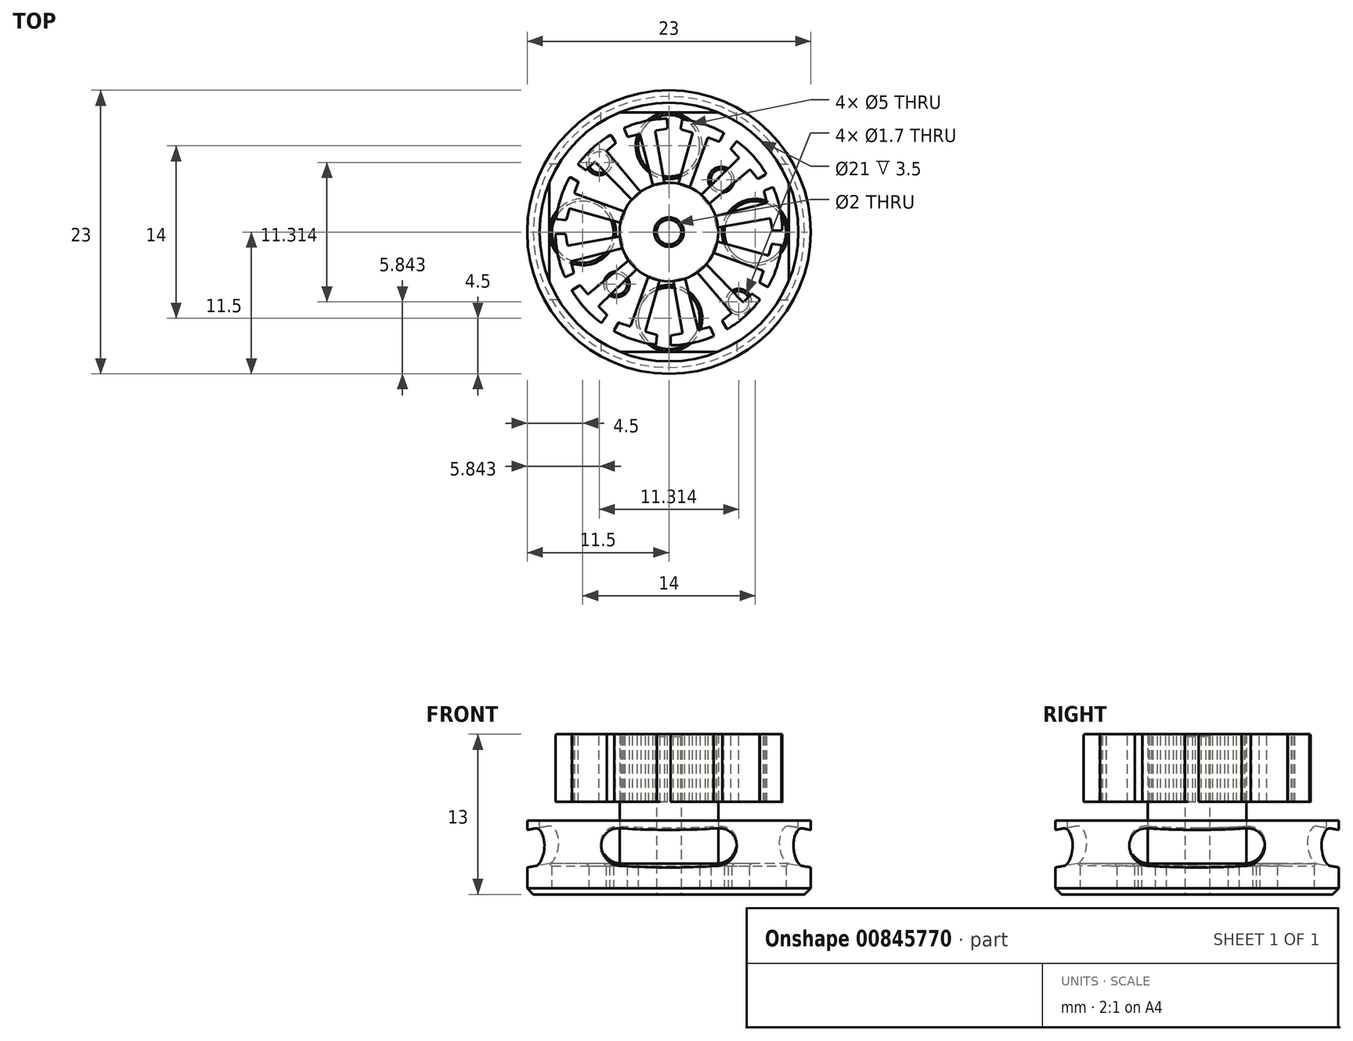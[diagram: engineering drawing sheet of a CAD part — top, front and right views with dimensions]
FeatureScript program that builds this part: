
annotation { "Feature Type Name" : "Feature", "Feature Type Description" : "" }
export const myFeature = defineFeature(function(context is Context, id is Id, definition is map)
    precondition{}
    {
        {
            var Q0;
            Q0=qCreatedBy(makeId("Top.planeOp"),FACE);
            var sketch = newSketch(context, id + "F0", { "sketchPlane" : qUnion([Q0])});
            skCircle(sketch, "E0", {"center": v(0, 0) * mm, "radius": 11.5 * mm});
            skSolve(sketch);
        }
        {
            var Q0;
            Q0 = qSketchRegion(id + "F0", true);
            extrude(context, id + "F1", {"entities" : qUnion([Q0]), "depth" : 6 * mm, "offsetDistance" : 25 * mm});
        }
        {
            var Q0;
            Q0=makeQuery(id+"F1.opExtrude","CAP_FACE",FACE,{"disambiguationData":[OSD([sQuery(id+"F0.wireOp",EDGE,"E0")])],"isStart":true});
            var sketch = newSketch(context, id + "F2", { "sketchPlane" : qUnion([Q0])});
            skCircle(sketch, "E1", {"center": v(0, 0) * mm, "radius": 1 * mm});
            skSolve(sketch);
        }
        {
            var Q0;
            Q0=makeQuery(id+"F1.opExtrude","CAP_EDGE",EDGE,{"disambiguationData":[OSD([sQuery(id+"F0.wireOp",EDGE,"E0")])],"isStart":true});
            chamfer(context, id + "F3", {"entities" : qUnion([Q0]), "width" : .5 * mm, "tangentPropagation" : true});
        }
        {
            var Q0;
            Q0=makeQuery(id+"F1.opExtrude","CAP_FACE",FACE,{"disambiguationData":[OSD([sQuery(id+"F0.wireOp",EDGE,"E0")])],"isStart":false});
            var sketch = newSketch(context, id + "F4", { "sketchPlane" : qUnion([Q0])});
            skCircle(sketch, "E2", {"center": v(0, 0) * mm, "radius": 10.5 * mm});
            skSolve(sketch);
        }
        {
            var Q0;
            Q0 = qSketchRegion(id + "F4", true);
            extrude(context, id + "F5", {"entities" : qUnion([Q0]), "operationType" : NewBodyOperationType.REMOVE, "oppositeDirection" : true, "depth" : 3.5 * mm, "offsetDistance" : 25 * mm});
        }
        {
            var Q0;
            Q0 = qSketchRegion(id + "F2", true);
            extrude(context, id + "F6", {"entities" : qUnion([Q0]), "operationType" : NewBodyOperationType.REMOVE, "endBound" : BoundingType.THROUGH_ALL, "oppositeDirection" : true, "depth" : 25 * mm, "offsetDistance" : 25 * mm});
        }
        {
            var Q0;
            Q0=makeQuery(id+"F1.opExtrude","CAP_FACE",FACE,{"disambiguationData":[OSD([sQuery(id+"F0.wireOp",EDGE,"E0")])],"isStart":true});
            var sketch = newSketch(context, id + "F7", { "sketchPlane" : qUnion([Q0])});
            skCircle(sketch, "E3", {"center": v(0, 7) * mm, "radius": 2.5 * mm});
            skCircle(sketch, "E4.1.0", {"center": v(-7, 0) * mm, "radius": 2.5 * mm});
            skCircle(sketch, "E4.2.0", {"center": v(0, -7) * mm, "radius": 2.5 * mm});
            skPoint(sketch, "E4.center", {"position": v(0, 0) * mm});
            skCircle(sketch, "E5.1.3.0", {"center": v(7, 0) * mm, "radius": 2.5 * mm});
            skSolve(sketch);
        }
        {
            var Q0;
            Q0 = qSketchRegion(id + "F7", true);
            extrude(context, id + "F8", {"entities" : qUnion([Q0]), "operationType" : NewBodyOperationType.REMOVE, "endBound" : BoundingType.THROUGH_ALL, "oppositeDirection" : true, "depth" : 25 * mm, "offsetDistance" : 25 * mm});
        }
        {
            var Q0;
            Q0=makeQuery(id+"F1.opExtrude","CAP_FACE",FACE,{"disambiguationData":[OSD([sQuery(id+"F0.wireOp",EDGE,"E0")])],"isStart":true});
            var sketch = newSketch(context, id + "F9", { "sketchPlane" : qUnion([Q0])});
            skCircle(sketch, "E6", {"center": v(4.24, -4.24) * mm, "radius": 0.85 * mm});
            skLineSegment(sketch, "E7", {"start": v(0, 0) * mm, "end": v(4.24, -4.24) * mm});
            skCircle(sketch, "E8.1.0", {"center": v(-4.24, 4.24) * mm, "radius": 0.85 * mm});
            skPoint(sketch, "E8.center", {"position": v(0, 0) * mm});
            skCircle(sketch, "E9", {"center": v(5.66, 5.66) * mm, "radius": 0.85 * mm});
            skLineSegment(sketch, "E10", {"start": v(0, 0) * mm, "end": v(5.66, 5.66) * mm});
            skCircle(sketch, "E11.1.0", {"center": v(-5.66, -5.66) * mm, "radius": 0.85 * mm});
            skSolve(sketch);
        }
        {
            var Q0;
            Q0=makeQuery(id+"F9.imprint","IMPRINT",FACE,{"disambiguationData":[TD([[makeQuery(id+"F9.imprint","IMPRINT",EDGE,{"derivedFrom":sQuery(id+"F9.wireOp",EDGE,"E8.1.0")}),1.0]])]});
            var Q1;
            Q1=makeQuery(id+"F9.imprint","IMPRINT",FACE,{"disambiguationData":[TD([[makeQuery(id+"F9.imprint","IMPRINT",EDGE,{"derivedFrom":sQuery(id+"F9.wireOp",EDGE,"E9")}),1.0]])]});
            var Q2;
            Q2=makeQuery(id+"F9.imprint","IMPRINT",FACE,{"disambiguationData":[TD([[makeQuery(id+"F9.imprint","IMPRINT",EDGE,{"derivedFrom":sQuery(id+"F9.wireOp",EDGE,"E6")}),1.0]])]});
            var Q3;
            Q3=makeQuery(id+"F9.imprint","IMPRINT",FACE,{"disambiguationData":[TD([[makeQuery(id+"F9.imprint","IMPRINT",EDGE,{"derivedFrom":sQuery(id+"F9.wireOp",EDGE,"E11.1.0")}),1.0]])]});
            var Q4;
            Q4=sQuery(id+"F9.wireOp",EDGE,"E6");
            extrude(context, id + "F10", {"entities" : qUnion([Q0, Q1, Q2, Q3]), "operationType" : NewBodyOperationType.REMOVE, "surfaceEntities" : qUnion([Q4]), "endBound" : BoundingType.THROUGH_ALL, "oppositeDirection" : true, "depth" : 25 * mm, "offsetDistance" : 25 * mm});
        }
        {
            var Q0;
            Q0=makeQuery(id+"F6.boolean.opBoolean","COPY",EDGE,{"derivedFrom":makeQuery(id+"F6.opExtrude","CAP_EDGE",EDGE,{"disambiguationData":[OSD([sQuery(id+"F2.wireOp",EDGE,"E1")])],"isStart":true})});
            var Q1;
            Q1=makeQuery(id+"F10.boolean.opBoolean","COPY",EDGE,{"derivedFrom":makeQuery(id+"F10.opExtrude","CAP_EDGE",EDGE,{"disambiguationData":[OSD([sQuery(id+"F9.wireOp",EDGE,"E6")])],"isStart":true})});
            var Q2;
            Q2=makeQuery(id+"F8.boolean.opBoolean","COPY",EDGE,{"derivedFrom":makeQuery(id+"F8.opExtrude","CAP_EDGE",EDGE,{"disambiguationData":[OSD([sQuery(id+"F7.wireOp",EDGE,"E5.1.3.0")])],"isStart":true})});
            var Q3;
            Q3=makeQuery(id+"F8.boolean.opBoolean","COPY",EDGE,{"derivedFrom":makeQuery(id+"F8.opExtrude","CAP_EDGE",EDGE,{"disambiguationData":[OSD([sQuery(id+"F7.wireOp",EDGE,"E3")])],"isStart":true})});
            var Q4;
            Q4=makeQuery(id+"F10.boolean.opBoolean","COPY",EDGE,{"derivedFrom":makeQuery(id+"F10.opExtrude","CAP_EDGE",EDGE,{"disambiguationData":[OSD([sQuery(id+"F9.wireOp",EDGE,"E8.1.0")])],"isStart":true})});
            var Q5;
            Q5=makeQuery(id+"F8.boolean.opBoolean","COPY",EDGE,{"derivedFrom":makeQuery(id+"F8.opExtrude","CAP_EDGE",EDGE,{"disambiguationData":[OSD([sQuery(id+"F7.wireOp",EDGE,"E4.1.0")])],"isStart":true})});
            var Q6;
            Q6=makeQuery(id+"F8.boolean.opBoolean","COPY",EDGE,{"derivedFrom":makeQuery(id+"F8.opExtrude","CAP_EDGE",EDGE,{"disambiguationData":[OSD([sQuery(id+"F7.wireOp",EDGE,"E4.2.0")])],"isStart":true})});
            var Q7;
            Q7=makeQuery(id+"F8.boolean.opBoolean","INTERSECT",EDGE,{"derivedFrom":[makeQuery(id+"F5.boolean.opBoolean","COPY",FACE,{"derivedFrom":makeQuery(id+"F5.opExtrude","CAP_FACE",FACE,{"disambiguationData":[OSD([sQuery(id+"F4.wireOp",EDGE,"E2")])],"isStart":false})}),makeQuery(id+"F8.opExtrude","SWEPT_FACE",FACE,{"disambiguationData":[OSD([sQuery(id+"F7.wireOp",EDGE,"E4.1.0")])]})]});
            var Q8;
            Q8=makeQuery(id+"F10.boolean.opBoolean","INTERSECT",EDGE,{"derivedFrom":[makeQuery(id+"F5.boolean.opBoolean","COPY",FACE,{"derivedFrom":makeQuery(id+"F5.opExtrude","CAP_FACE",FACE,{"disambiguationData":[OSD([sQuery(id+"F4.wireOp",EDGE,"E2")])],"isStart":false})}),makeQuery(id+"F10.opExtrude","SWEPT_FACE",FACE,{"disambiguationData":[OSD([sQuery(id+"F9.wireOp",EDGE,"E8.1.0")])]})]});
            var Q9;
            Q9=makeQuery(id+"F8.boolean.opBoolean","INTERSECT",EDGE,{"derivedFrom":[makeQuery(id+"F5.boolean.opBoolean","COPY",FACE,{"derivedFrom":makeQuery(id+"F5.opExtrude","CAP_FACE",FACE,{"disambiguationData":[OSD([sQuery(id+"F4.wireOp",EDGE,"E2")])],"isStart":false})}),makeQuery(id+"F8.opExtrude","SWEPT_FACE",FACE,{"disambiguationData":[OSD([sQuery(id+"F7.wireOp",EDGE,"E4.2.0")])]})]});
            var Q10;
            Q10=makeQuery(id+"F10.boolean.opBoolean","INTERSECT",EDGE,{"derivedFrom":[makeQuery(id+"F5.boolean.opBoolean","COPY",FACE,{"derivedFrom":makeQuery(id+"F5.opExtrude","CAP_FACE",FACE,{"disambiguationData":[OSD([sQuery(id+"F4.wireOp",EDGE,"E2")])],"isStart":false})}),makeQuery(id+"F10.opExtrude","SWEPT_FACE",FACE,{"disambiguationData":[OSD([sQuery(id+"F9.wireOp",EDGE,"E6")])]})]});
            var Q11;
            Q11=makeQuery(id+"F8.boolean.opBoolean","INTERSECT",EDGE,{"derivedFrom":[makeQuery(id+"F5.boolean.opBoolean","COPY",FACE,{"derivedFrom":makeQuery(id+"F5.opExtrude","CAP_FACE",FACE,{"disambiguationData":[OSD([sQuery(id+"F4.wireOp",EDGE,"E2")])],"isStart":false})}),makeQuery(id+"F8.opExtrude","SWEPT_FACE",FACE,{"disambiguationData":[OSD([sQuery(id+"F7.wireOp",EDGE,"E5.1.3.0")])]})]});
            var Q12;
            Q12=makeQuery(id+"F8.boolean.opBoolean","INTERSECT",EDGE,{"derivedFrom":[makeQuery(id+"F5.boolean.opBoolean","COPY",FACE,{"derivedFrom":makeQuery(id+"F5.opExtrude","CAP_FACE",FACE,{"disambiguationData":[OSD([sQuery(id+"F4.wireOp",EDGE,"E2")])],"isStart":false})}),makeQuery(id+"F8.opExtrude","SWEPT_FACE",FACE,{"disambiguationData":[OSD([sQuery(id+"F7.wireOp",EDGE,"E3")])]})]});
            var Q13;
            Q13=makeQuery(id+"F10.boolean.opBoolean","COPY",EDGE,{"derivedFrom":makeQuery(id+"F10.opExtrude","CAP_EDGE",EDGE,{"disambiguationData":[OSD([sQuery(id+"F9.wireOp",EDGE,"E11.1.0")])],"isStart":true})});
            var Q14;
            Q14=makeQuery(id+"F10.boolean.opBoolean","COPY",EDGE,{"derivedFrom":makeQuery(id+"F10.opExtrude","CAP_EDGE",EDGE,{"disambiguationData":[OSD([sQuery(id+"F9.wireOp",EDGE,"E9")])],"isStart":true})});
            var Q15;
            Q15=makeQuery(id+"F10.boolean.opBoolean","INTERSECT",EDGE,{"derivedFrom":[makeQuery(id+"F5.boolean.opBoolean","COPY",FACE,{"derivedFrom":makeQuery(id+"F5.opExtrude","CAP_FACE",FACE,{"disambiguationData":[OSD([sQuery(id+"F4.wireOp",EDGE,"E2")])],"isStart":false})}),makeQuery(id+"F10.opExtrude","SWEPT_FACE",FACE,{"disambiguationData":[OSD([sQuery(id+"F9.wireOp",EDGE,"E9")])]})]});
            var Q16;
            Q16=makeQuery(id+"F10.boolean.opBoolean","INTERSECT",EDGE,{"derivedFrom":[makeQuery(id+"F5.boolean.opBoolean","COPY",FACE,{"derivedFrom":makeQuery(id+"F5.opExtrude","CAP_FACE",FACE,{"disambiguationData":[OSD([sQuery(id+"F4.wireOp",EDGE,"E2")])],"isStart":false})}),makeQuery(id+"F10.opExtrude","SWEPT_FACE",FACE,{"disambiguationData":[OSD([sQuery(id+"F9.wireOp",EDGE,"E11.1.0")])]})]});
            chamfer(context, id + "F11", {"entities" : qUnion([Q0, Q1, Q2, Q3, Q4, Q5, Q6, Q7, Q8, Q9, Q10, Q11, Q12, Q13, Q14, Q15, Q16]), "width" : .2 * mm, "tangentPropagation" : true});
        }
        {
            var Q0;
            Q0=makeQuery(id+"F1.opExtrude","CAP_FACE",FACE,{"disambiguationData":[OSD([sQuery(id+"F0.wireOp",EDGE,"E0")])],"isStart":true});
            var sketch = newSketch(context, id + "F12", { "sketchPlane" : qUnion([Q0])});
            skCircle(sketch, "E12", {"center": v(0, 0) * mm, "radius": 4 * mm});
            skSolve(sketch);
        }
        {
            var Q0;
            Q0 = qSketchRegion(id + "F12", true);
            extrude(context, id + "F13", {"entities" : qUnion([Q0]), "operationType" : NewBodyOperationType.ADD, "depth" : -13 * mm, "offsetDistance" : 25 * mm});
        }
        {
            var Q0;
            Q0 = qSketchRegion(id + "F2", true);
            extrude(context, id + "F14", {"entities" : qUnion([Q0]), "operationType" : NewBodyOperationType.REMOVE, "endBound" : BoundingType.THROUGH_ALL, "oppositeDirection" : true, "depth" : 25 * mm, "offsetDistance" : 25 * mm});
        }
        {
            var Q0;
            Q0=makeQuery(id+"F14.boolean.opBoolean","COPY",EDGE,{"derivedFrom":makeQuery(id+"F14.opExtrude","CAP_EDGE",EDGE,{"disambiguationData":[OSD([sQuery(id+"F2.wireOp",EDGE,"E1")])],"isStart":true})});
            var Q1;
            Q1=makeQuery(id+"F14.boolean.opBoolean","INTERSECT",EDGE,{"derivedFrom":[makeQuery(id+"F13.opExtrude","CAP_FACE",FACE,{"disambiguationData":[OSD([sQuery(id+"F12.wireOp",EDGE,"E12")])],"isStart":false}),makeQuery(id+"F14.opExtrude","SWEPT_FACE",FACE,{"disambiguationData":[OSD([sQuery(id+"F2.wireOp",EDGE,"E1")])]})]});
            chamfer(context, id + "F15", {"entities" : qUnion([Q0, Q1]), "width" : .2 * mm, "tangentPropagation" : true});
        }
        {
            var Q0;
            Q0=makeQuery(id+"F13.opExtrude","CAP_FACE",FACE,{"disambiguationData":[OSD([sQuery(id+"F12.wireOp",EDGE,"E12")])],"isStart":false});
            var sketch = newSketch(context, id + "F16", { "sketchPlane" : qUnion([Q0])});
            skLineSegment(sketch, "E13", {"start": v(-3.84, 0.73) * mm, "end": v(-7.98, 1.9) * mm});
            skLineSegment(sketch, "E14", {"start": v(-8.1, 1.83) * mm, "end": v(-8.32, 1.04) * mm});
            skLineSegment(sketch, "E15", {"start": v(-7.64, 3.25) * mm, "end": v(-7.37, 4.01) * mm});
            skArc(sketch, "E16", {"start": v(-8.08, 4.4) * mm, "mid": v(-8.76, 2.82) * mm, "end": v(-9.13, 1.15) * mm});
            skLineSegment(sketch, "E17", {"start": v(-8.43, 0.97) * mm, "end": v(-9.04, 1.04) * mm});
            skLineSegment(sketch, "E18", {"start": v(-7.41, 4.13) * mm, "end": v(-7.95, 4.43) * mm});
            skLineSegment(sketch, "E19", {"start": v(-3.54, 1.65) * mm, "end": v(-3.84, 0.73) * mm});
            skLineSegment(sketch, "E20", {"start": v(-7.58, 3.12) * mm, "end": v(-3.54, 1.65) * mm});
            skPoint(sketch, "E21.visualSharp", {"position": v(-9.14, 1.05) * mm});
            skArc(sketch, "E21.filletArc", {"start": v(-9.13, 1.15) * mm, "mid": v(-9.1, 1.08) * mm, "end": v(-9.04, 1.04) * mm});
            skPoint(sketch, "E22.visualSharp", {"position": v(-8.34, 0.96) * mm});
            skArc(sketch, "E22.filletArc", {"start": v(-8.43, 0.97) * mm, "mid": v(-8.36, 0.99) * mm, "end": v(-8.32, 1.04) * mm});
            skPoint(sketch, "E23.visualSharp", {"position": v(-8.07, 1.93) * mm});
            skArc(sketch, "E23.filletArc", {"start": v(-7.98, 1.9) * mm, "mid": v(-8.05, 1.89) * mm, "end": v(-8.1, 1.83) * mm});
            skPoint(sketch, "E24.visualSharp", {"position": v(-7.68, 3.15) * mm});
            skArc(sketch, "E24.filletArc", {"start": v(-7.64, 3.25) * mm, "mid": v(-7.64, 3.17) * mm, "end": v(-7.58, 3.12) * mm});
            skPoint(sketch, "E25.visualSharp", {"position": v(-7.34, 4.1) * mm});
            skArc(sketch, "E25.filletArc", {"start": v(-7.37, 4.01) * mm, "mid": v(-7.37, 4.08) * mm, "end": v(-7.41, 4.13) * mm});
            skPoint(sketch, "E26.visualSharp", {"position": v(-8.04, 4.48) * mm});
            skArc(sketch, "E26.filletArc", {"start": v(-7.95, 4.43) * mm, "mid": v(-8.02, 4.44) * mm, "end": v(-8.08, 4.4) * mm});
            skLineSegment(sketch, "E27.1.0", {"start": v(-8.13, -1.1) * mm, "end": v(-3.9, -0.35) * mm});
            skArc(sketch, "E27.1.1", {"start": v(-7.86, -2.35) * mm, "mid": v(-7.92, -2.4) * mm, "end": v(-7.93, -2.47) * mm});
            skLineSegment(sketch, "E27.1.2", {"start": v(-3.9, -0.35) * mm, "end": v(-3.7, -1.28) * mm});
            skLineSegment(sketch, "E27.1.3", {"start": v(-3.7, -1.28) * mm, "end": v(-7.86, -2.35) * mm});
            skLineSegment(sketch, "E27.1.4", {"start": v(-7.93, -2.47) * mm, "end": v(-7.73, -3.26) * mm});
            skPoint(sketch, "E27.1.5", {"position": v(-7.7, -3.34) * mm});
            skArc(sketch, "E27.1.6", {"start": v(-7.79, -3.37) * mm, "mid": v(-7.74, -3.33) * mm, "end": v(-7.73, -3.26) * mm});
            skLineSegment(sketch, "E27.1.7", {"start": v(-7.79, -3.37) * mm, "end": v(-8.35, -3.62) * mm});
            skArc(sketch, "E27.1.8", {"start": v(-8.48, -3.56) * mm, "mid": v(-8.43, -3.62) * mm, "end": v(-8.35, -3.62) * mm});
            skArc(sketch, "E27.1.9", {"start": v(-9.2, -0.24) * mm, "mid": v(-9, -1.93) * mm, "end": v(-8.48, -3.56) * mm});
            skArc(sketch, "E27.1.10", {"start": v(-9.1, -0.14) * mm, "mid": v(-9.17, -0.17) * mm, "end": v(-9.2, -0.24) * mm});
            skLineSegment(sketch, "E27.1.11", {"start": v(-8.48, -0.13) * mm, "end": v(-9.1, -0.14) * mm});
            skArc(sketch, "E27.1.12", {"start": v(-8.38, -0.2) * mm, "mid": v(-8.42, -0.15) * mm, "end": v(-8.48, -0.13) * mm});
            skLineSegment(sketch, "E27.1.13", {"start": v(-8.24, -1.01) * mm, "end": v(-8.38, -0.2) * mm});
            skArc(sketch, "E27.1.14", {"start": v(-8.24, -1.01) * mm, "mid": v(-8.2, -1.08) * mm, "end": v(-8.13, -1.1) * mm});
            skLineSegment(sketch, "E27.2.0", {"start": v(-6.5, -5) * mm, "end": v(-3.2, -2.25) * mm});
            skArc(sketch, "E27.2.1", {"start": v(-5.63, -5.96) * mm, "mid": v(-5.66, -6.03) * mm, "end": v(-5.63, -6.1) * mm});
            skLineSegment(sketch, "E27.2.2", {"start": v(-3.2, -2.25) * mm, "end": v(-2.55, -2.96) * mm});
            skLineSegment(sketch, "E27.2.3", {"start": v(-2.55, -2.96) * mm, "end": v(-5.63, -5.96) * mm});
            skLineSegment(sketch, "E27.2.4", {"start": v(-5.63, -6.1) * mm, "end": v(-5.07, -6.68) * mm});
            skPoint(sketch, "E27.2.5", {"position": v(-5, -6.75) * mm});
            skArc(sketch, "E27.2.6", {"start": v(-5.06, -6.81) * mm, "mid": v(-5.04, -6.75) * mm, "end": v(-5.07, -6.68) * mm});
            skLineSegment(sketch, "E27.2.7", {"start": v(-5.06, -6.81) * mm, "end": v(-5.42, -7.3) * mm});
            skArc(sketch, "E27.2.8", {"start": v(-5.56, -7.33) * mm, "mid": v(-5.49, -7.35) * mm, "end": v(-5.42, -7.3) * mm});
            skArc(sketch, "E27.2.9", {"start": v(-7.85, -4.8) * mm, "mid": v(-6.82, -6.17) * mm, "end": v(-5.56, -7.33) * mm});
            skArc(sketch, "E27.2.10", {"start": v(-7.81, -4.67) * mm, "mid": v(-7.86, -4.73) * mm, "end": v(-7.85, -4.8) * mm});
            skLineSegment(sketch, "E27.2.11", {"start": v(-7.28, -4.35) * mm, "end": v(-7.81, -4.67) * mm});
            skArc(sketch, "E27.2.12", {"start": v(-7.16, -4.37) * mm, "mid": v(-7.22, -4.34) * mm, "end": v(-7.28, -4.35) * mm});
            skLineSegment(sketch, "E27.2.13", {"start": v(-6.63, -5) * mm, "end": v(-7.16, -4.37) * mm});
            skArc(sketch, "E27.2.14", {"start": v(-6.63, -5) * mm, "mid": v(-6.56, -5.03) * mm, "end": v(-6.5, -5) * mm});
            skLineSegment(sketch, "E28.1.3.0", {"start": v(-3.12, -7.58) * mm, "end": v(-1.65, -3.54) * mm});
            skArc(sketch, "E28.3.3.0", {"start": v(-1.9, -7.98) * mm, "mid": v(-1.89, -8.05) * mm, "end": v(-1.83, -8.1) * mm});
            skLineSegment(sketch, "E28.7.3.0", {"start": v(-1.65, -3.54) * mm, "end": v(-0.73, -3.84) * mm});
            skLineSegment(sketch, "E28.10.3.0", {"start": v(-0.73, -3.84) * mm, "end": v(-1.9, -7.98) * mm});
            skLineSegment(sketch, "E28.13.3.0", {"start": v(-1.83, -8.1) * mm, "end": v(-1.04, -8.32) * mm});
            skPoint(sketch, "E28.16.3.0", {"position": v(-0.96, -8.34) * mm});
            skArc(sketch, "E28.17.3.0", {"start": v(-0.97, -8.43) * mm, "mid": v(-0.99, -8.36) * mm, "end": v(-1.04, -8.32) * mm});
            skLineSegment(sketch, "E28.21.3.0", {"start": v(-0.97, -8.43) * mm, "end": v(-1.04, -9.04) * mm});
            skArc(sketch, "E28.24.3.0", {"start": v(-1.15, -9.13) * mm, "mid": v(-1.08, -9.1) * mm, "end": v(-1.04, -9.04) * mm});
            skArc(sketch, "E28.28.3.0", {"start": v(-4.4, -8.08) * mm, "mid": v(-2.82, -8.76) * mm, "end": v(-1.15, -9.13) * mm});
            skArc(sketch, "E28.32.3.0", {"start": v(-4.43, -7.95) * mm, "mid": v(-4.44, -8.02) * mm, "end": v(-4.4, -8.08) * mm});
            skLineSegment(sketch, "E28.36.3.0", {"start": v(-4.13, -7.41) * mm, "end": v(-4.43, -7.95) * mm});
            skArc(sketch, "E28.39.3.0", {"start": v(-4.01, -7.37) * mm, "mid": v(-4.08, -7.37) * mm, "end": v(-4.13, -7.41) * mm});
            skLineSegment(sketch, "E28.43.3.0", {"start": v(-3.25, -7.64) * mm, "end": v(-4.01, -7.37) * mm});
            skArc(sketch, "E28.46.3.0", {"start": v(-3.25, -7.64) * mm, "mid": v(-3.17, -7.64) * mm, "end": v(-3.12, -7.58) * mm});
            skLineSegment(sketch, "E28.1.4.0", {"start": v(1.1, -8.13) * mm, "end": v(0.35, -3.9) * mm});
            skArc(sketch, "E28.3.4.0", {"start": v(2.35, -7.86) * mm, "mid": v(2.4, -7.92) * mm, "end": v(2.47, -7.93) * mm});
            skLineSegment(sketch, "E28.7.4.0", {"start": v(0.35, -3.9) * mm, "end": v(1.28, -3.7) * mm});
            skLineSegment(sketch, "E28.10.4.0", {"start": v(1.28, -3.7) * mm, "end": v(2.35, -7.86) * mm});
            skLineSegment(sketch, "E28.13.4.0", {"start": v(2.47, -7.93) * mm, "end": v(3.26, -7.73) * mm});
            skPoint(sketch, "E28.16.4.0", {"position": v(3.34, -7.7) * mm});
            skArc(sketch, "E28.17.4.0", {"start": v(3.37, -7.79) * mm, "mid": v(3.33, -7.74) * mm, "end": v(3.26, -7.73) * mm});
            skLineSegment(sketch, "E28.21.4.0", {"start": v(3.37, -7.79) * mm, "end": v(3.62, -8.35) * mm});
            skArc(sketch, "E28.24.4.0", {"start": v(3.56, -8.48) * mm, "mid": v(3.62, -8.43) * mm, "end": v(3.62, -8.35) * mm});
            skArc(sketch, "E28.28.4.0", {"start": v(0.24, -9.2) * mm, "mid": v(1.93, -9) * mm, "end": v(3.56, -8.48) * mm});
            skArc(sketch, "E28.32.4.0", {"start": v(0.14, -9.1) * mm, "mid": v(0.17, -9.17) * mm, "end": v(0.24, -9.2) * mm});
            skLineSegment(sketch, "E28.36.4.0", {"start": v(0.13, -8.48) * mm, "end": v(0.14, -9.1) * mm});
            skArc(sketch, "E28.39.4.0", {"start": v(0.2, -8.38) * mm, "mid": v(0.15, -8.42) * mm, "end": v(0.13, -8.48) * mm});
            skLineSegment(sketch, "E28.43.4.0", {"start": v(1.01, -8.24) * mm, "end": v(0.2, -8.38) * mm});
            skArc(sketch, "E28.46.4.0", {"start": v(1.01, -8.24) * mm, "mid": v(1.08, -8.2) * mm, "end": v(1.1, -8.13) * mm});
            skLineSegment(sketch, "E28.1.5.0", {"start": v(5, -6.5) * mm, "end": v(2.25, -3.2) * mm});
            skArc(sketch, "E28.3.5.0", {"start": v(5.96, -5.63) * mm, "mid": v(6.03, -5.66) * mm, "end": v(6.1, -5.63) * mm});
            skLineSegment(sketch, "E28.7.5.0", {"start": v(2.25, -3.2) * mm, "end": v(2.96, -2.55) * mm});
            skLineSegment(sketch, "E28.10.5.0", {"start": v(2.96, -2.55) * mm, "end": v(5.96, -5.63) * mm});
            skLineSegment(sketch, "E28.13.5.0", {"start": v(6.1, -5.63) * mm, "end": v(6.68, -5.07) * mm});
            skPoint(sketch, "E28.16.5.0", {"position": v(6.75, -5) * mm});
            skArc(sketch, "E28.17.5.0", {"start": v(6.81, -5.06) * mm, "mid": v(6.75, -5.04) * mm, "end": v(6.68, -5.07) * mm});
            skLineSegment(sketch, "E28.21.5.0", {"start": v(6.81, -5.06) * mm, "end": v(7.3, -5.42) * mm});
            skArc(sketch, "E28.24.5.0", {"start": v(7.33, -5.56) * mm, "mid": v(7.35, -5.49) * mm, "end": v(7.3, -5.42) * mm});
            skArc(sketch, "E28.28.5.0", {"start": v(4.8, -7.85) * mm, "mid": v(6.17, -6.82) * mm, "end": v(7.33, -5.56) * mm});
            skArc(sketch, "E28.32.5.0", {"start": v(4.67, -7.81) * mm, "mid": v(4.73, -7.86) * mm, "end": v(4.8, -7.85) * mm});
            skLineSegment(sketch, "E28.36.5.0", {"start": v(4.35, -7.28) * mm, "end": v(4.67, -7.81) * mm});
            skArc(sketch, "E28.39.5.0", {"start": v(4.37, -7.16) * mm, "mid": v(4.34, -7.22) * mm, "end": v(4.35, -7.28) * mm});
            skLineSegment(sketch, "E28.43.5.0", {"start": v(5, -6.63) * mm, "end": v(4.37, -7.16) * mm});
            skArc(sketch, "E28.46.5.0", {"start": v(5, -6.63) * mm, "mid": v(5.03, -6.56) * mm, "end": v(5, -6.5) * mm});
            skLineSegment(sketch, "E28.1.6.0", {"start": v(7.58, -3.12) * mm, "end": v(3.54, -1.65) * mm});
            skArc(sketch, "E28.3.6.0", {"start": v(7.98, -1.9) * mm, "mid": v(8.05, -1.89) * mm, "end": v(8.1, -1.83) * mm});
            skLineSegment(sketch, "E28.7.6.0", {"start": v(3.54, -1.65) * mm, "end": v(3.84, -0.73) * mm});
            skLineSegment(sketch, "E28.10.6.0", {"start": v(3.84, -0.73) * mm, "end": v(7.98, -1.9) * mm});
            skLineSegment(sketch, "E28.13.6.0", {"start": v(8.1, -1.83) * mm, "end": v(8.32, -1.04) * mm});
            skPoint(sketch, "E28.16.6.0", {"position": v(8.34, -0.96) * mm});
            skArc(sketch, "E28.17.6.0", {"start": v(8.43, -0.97) * mm, "mid": v(8.36, -0.99) * mm, "end": v(8.32, -1.04) * mm});
            skLineSegment(sketch, "E28.21.6.0", {"start": v(8.43, -0.97) * mm, "end": v(9.04, -1.04) * mm});
            skArc(sketch, "E28.24.6.0", {"start": v(9.13, -1.15) * mm, "mid": v(9.1, -1.08) * mm, "end": v(9.04, -1.04) * mm});
            skArc(sketch, "E28.28.6.0", {"start": v(8.08, -4.4) * mm, "mid": v(8.76, -2.82) * mm, "end": v(9.13, -1.15) * mm});
            skArc(sketch, "E28.32.6.0", {"start": v(7.95, -4.43) * mm, "mid": v(8.02, -4.44) * mm, "end": v(8.08, -4.4) * mm});
            skLineSegment(sketch, "E28.36.6.0", {"start": v(7.41, -4.13) * mm, "end": v(7.95, -4.43) * mm});
            skArc(sketch, "E28.39.6.0", {"start": v(7.37, -4.01) * mm, "mid": v(7.37, -4.08) * mm, "end": v(7.41, -4.13) * mm});
            skLineSegment(sketch, "E28.43.6.0", {"start": v(7.64, -3.25) * mm, "end": v(7.37, -4.01) * mm});
            skArc(sketch, "E28.46.6.0", {"start": v(7.64, -3.25) * mm, "mid": v(7.64, -3.17) * mm, "end": v(7.58, -3.12) * mm});
            skLineSegment(sketch, "E28.1.7.0", {"start": v(8.13, 1.1) * mm, "end": v(3.9, 0.35) * mm});
            skArc(sketch, "E28.3.7.0", {"start": v(7.86, 2.35) * mm, "mid": v(7.92, 2.4) * mm, "end": v(7.93, 2.47) * mm});
            skLineSegment(sketch, "E28.7.7.0", {"start": v(3.9, 0.35) * mm, "end": v(3.7, 1.28) * mm});
            skLineSegment(sketch, "E28.10.7.0", {"start": v(3.7, 1.28) * mm, "end": v(7.86, 2.35) * mm});
            skLineSegment(sketch, "E28.13.7.0", {"start": v(7.93, 2.47) * mm, "end": v(7.73, 3.26) * mm});
            skPoint(sketch, "E28.16.7.0", {"position": v(7.7, 3.34) * mm});
            skArc(sketch, "E28.17.7.0", {"start": v(7.79, 3.37) * mm, "mid": v(7.74, 3.33) * mm, "end": v(7.73, 3.26) * mm});
            skLineSegment(sketch, "E28.21.7.0", {"start": v(7.79, 3.37) * mm, "end": v(8.35, 3.62) * mm});
            skArc(sketch, "E28.24.7.0", {"start": v(8.48, 3.56) * mm, "mid": v(8.43, 3.62) * mm, "end": v(8.35, 3.62) * mm});
            skArc(sketch, "E28.28.7.0", {"start": v(9.2, 0.24) * mm, "mid": v(9, 1.93) * mm, "end": v(8.48, 3.56) * mm});
            skArc(sketch, "E28.32.7.0", {"start": v(9.1, 0.14) * mm, "mid": v(9.17, 0.17) * mm, "end": v(9.2, 0.24) * mm});
            skLineSegment(sketch, "E28.36.7.0", {"start": v(8.48, 0.13) * mm, "end": v(9.1, 0.14) * mm});
            skArc(sketch, "E28.39.7.0", {"start": v(8.38, 0.2) * mm, "mid": v(8.42, 0.15) * mm, "end": v(8.48, 0.13) * mm});
            skLineSegment(sketch, "E28.43.7.0", {"start": v(8.24, 1.01) * mm, "end": v(8.38, 0.2) * mm});
            skArc(sketch, "E28.46.7.0", {"start": v(8.24, 1.01) * mm, "mid": v(8.2, 1.08) * mm, "end": v(8.13, 1.1) * mm});
            skLineSegment(sketch, "E28.1.8.0", {"start": v(6.5, 5) * mm, "end": v(3.2, 2.25) * mm});
            skArc(sketch, "E28.3.8.0", {"start": v(5.63, 5.96) * mm, "mid": v(5.66, 6.03) * mm, "end": v(5.63, 6.1) * mm});
            skLineSegment(sketch, "E28.7.8.0", {"start": v(3.2, 2.25) * mm, "end": v(2.55, 2.96) * mm});
            skLineSegment(sketch, "E28.10.8.0", {"start": v(2.55, 2.96) * mm, "end": v(5.63, 5.96) * mm});
            skLineSegment(sketch, "E28.13.8.0", {"start": v(5.63, 6.1) * mm, "end": v(5.07, 6.68) * mm});
            skPoint(sketch, "E28.16.8.0", {"position": v(5, 6.75) * mm});
            skArc(sketch, "E28.17.8.0", {"start": v(5.06, 6.81) * mm, "mid": v(5.04, 6.75) * mm, "end": v(5.07, 6.68) * mm});
            skLineSegment(sketch, "E28.21.8.0", {"start": v(5.06, 6.81) * mm, "end": v(5.42, 7.3) * mm});
            skArc(sketch, "E28.24.8.0", {"start": v(5.56, 7.33) * mm, "mid": v(5.49, 7.35) * mm, "end": v(5.42, 7.3) * mm});
            skArc(sketch, "E28.28.8.0", {"start": v(7.85, 4.8) * mm, "mid": v(6.82, 6.17) * mm, "end": v(5.56, 7.33) * mm});
            skArc(sketch, "E28.32.8.0", {"start": v(7.81, 4.67) * mm, "mid": v(7.86, 4.73) * mm, "end": v(7.85, 4.8) * mm});
            skLineSegment(sketch, "E28.36.8.0", {"start": v(7.28, 4.35) * mm, "end": v(7.81, 4.67) * mm});
            skArc(sketch, "E28.39.8.0", {"start": v(7.16, 4.37) * mm, "mid": v(7.22, 4.34) * mm, "end": v(7.28, 4.35) * mm});
            skLineSegment(sketch, "E28.43.8.0", {"start": v(6.63, 5) * mm, "end": v(7.16, 4.37) * mm});
            skArc(sketch, "E28.46.8.0", {"start": v(6.63, 5) * mm, "mid": v(6.56, 5.03) * mm, "end": v(6.5, 5) * mm});
            skLineSegment(sketch, "E28.1.9.0", {"start": v(3.12, 7.58) * mm, "end": v(1.65, 3.54) * mm});
            skArc(sketch, "E28.3.9.0", {"start": v(1.9, 7.98) * mm, "mid": v(1.89, 8.05) * mm, "end": v(1.83, 8.1) * mm});
            skLineSegment(sketch, "E28.7.9.0", {"start": v(1.65, 3.54) * mm, "end": v(0.73, 3.84) * mm});
            skLineSegment(sketch, "E28.10.9.0", {"start": v(0.73, 3.84) * mm, "end": v(1.9, 7.98) * mm});
            skLineSegment(sketch, "E28.13.9.0", {"start": v(1.83, 8.1) * mm, "end": v(1.04, 8.32) * mm});
            skPoint(sketch, "E28.16.9.0", {"position": v(0.96, 8.34) * mm});
            skArc(sketch, "E28.17.9.0", {"start": v(0.97, 8.43) * mm, "mid": v(0.99, 8.36) * mm, "end": v(1.04, 8.32) * mm});
            skLineSegment(sketch, "E28.21.9.0", {"start": v(0.97, 8.43) * mm, "end": v(1.04, 9.04) * mm});
            skArc(sketch, "E28.24.9.0", {"start": v(1.15, 9.13) * mm, "mid": v(1.08, 9.1) * mm, "end": v(1.04, 9.04) * mm});
            skArc(sketch, "E28.28.9.0", {"start": v(4.4, 8.08) * mm, "mid": v(2.82, 8.76) * mm, "end": v(1.15, 9.13) * mm});
            skArc(sketch, "E28.32.9.0", {"start": v(4.43, 7.95) * mm, "mid": v(4.44, 8.02) * mm, "end": v(4.4, 8.08) * mm});
            skLineSegment(sketch, "E28.36.9.0", {"start": v(4.13, 7.41) * mm, "end": v(4.43, 7.95) * mm});
            skArc(sketch, "E28.39.9.0", {"start": v(4.01, 7.37) * mm, "mid": v(4.08, 7.37) * mm, "end": v(4.13, 7.41) * mm});
            skLineSegment(sketch, "E28.43.9.0", {"start": v(3.25, 7.64) * mm, "end": v(4.01, 7.37) * mm});
            skArc(sketch, "E28.46.9.0", {"start": v(3.25, 7.64) * mm, "mid": v(3.17, 7.64) * mm, "end": v(3.12, 7.58) * mm});
            skLineSegment(sketch, "E28.1.10.0", {"start": v(-1.1, 8.13) * mm, "end": v(-0.35, 3.9) * mm});
            skArc(sketch, "E28.3.10.0", {"start": v(-2.35, 7.86) * mm, "mid": v(-2.4, 7.92) * mm, "end": v(-2.47, 7.93) * mm});
            skLineSegment(sketch, "E28.7.10.0", {"start": v(-0.35, 3.9) * mm, "end": v(-1.28, 3.7) * mm});
            skLineSegment(sketch, "E28.10.10.0", {"start": v(-1.28, 3.7) * mm, "end": v(-2.35, 7.86) * mm});
            skLineSegment(sketch, "E28.13.10.0", {"start": v(-2.47, 7.93) * mm, "end": v(-3.26, 7.73) * mm});
            skPoint(sketch, "E28.16.10.0", {"position": v(-3.34, 7.7) * mm});
            skArc(sketch, "E28.17.10.0", {"start": v(-3.37, 7.79) * mm, "mid": v(-3.33, 7.74) * mm, "end": v(-3.26, 7.73) * mm});
            skLineSegment(sketch, "E28.21.10.0", {"start": v(-3.37, 7.79) * mm, "end": v(-3.62, 8.35) * mm});
            skArc(sketch, "E28.24.10.0", {"start": v(-3.56, 8.48) * mm, "mid": v(-3.62, 8.43) * mm, "end": v(-3.62, 8.35) * mm});
            skArc(sketch, "E28.28.10.0", {"start": v(-0.24, 9.2) * mm, "mid": v(-1.93, 9) * mm, "end": v(-3.56, 8.48) * mm});
            skArc(sketch, "E28.32.10.0", {"start": v(-0.14, 9.1) * mm, "mid": v(-0.17, 9.17) * mm, "end": v(-0.24, 9.2) * mm});
            skLineSegment(sketch, "E28.36.10.0", {"start": v(-0.13, 8.48) * mm, "end": v(-0.14, 9.1) * mm});
            skArc(sketch, "E28.39.10.0", {"start": v(-0.2, 8.38) * mm, "mid": v(-0.15, 8.42) * mm, "end": v(-0.13, 8.48) * mm});
            skLineSegment(sketch, "E28.43.10.0", {"start": v(-1.01, 8.24) * mm, "end": v(-0.2, 8.38) * mm});
            skArc(sketch, "E28.46.10.0", {"start": v(-1.01, 8.24) * mm, "mid": v(-1.08, 8.2) * mm, "end": v(-1.1, 8.13) * mm});
            skLineSegment(sketch, "E28.1.11.0", {"start": v(-5, 6.5) * mm, "end": v(-2.25, 3.2) * mm});
            skArc(sketch, "E28.3.11.0", {"start": v(-5.96, 5.63) * mm, "mid": v(-6.03, 5.66) * mm, "end": v(-6.1, 5.63) * mm});
            skLineSegment(sketch, "E28.7.11.0", {"start": v(-2.25, 3.2) * mm, "end": v(-2.96, 2.55) * mm});
            skLineSegment(sketch, "E28.10.11.0", {"start": v(-2.96, 2.55) * mm, "end": v(-5.96, 5.63) * mm});
            skLineSegment(sketch, "E28.13.11.0", {"start": v(-6.1, 5.63) * mm, "end": v(-6.68, 5.07) * mm});
            skPoint(sketch, "E28.16.11.0", {"position": v(-6.75, 5) * mm});
            skArc(sketch, "E28.17.11.0", {"start": v(-6.81, 5.06) * mm, "mid": v(-6.75, 5.04) * mm, "end": v(-6.68, 5.07) * mm});
            skLineSegment(sketch, "E28.21.11.0", {"start": v(-6.81, 5.06) * mm, "end": v(-7.3, 5.42) * mm});
            skArc(sketch, "E28.24.11.0", {"start": v(-7.33, 5.56) * mm, "mid": v(-7.35, 5.49) * mm, "end": v(-7.3, 5.42) * mm});
            skArc(sketch, "E28.28.11.0", {"start": v(-4.8, 7.85) * mm, "mid": v(-6.17, 6.82) * mm, "end": v(-7.33, 5.56) * mm});
            skArc(sketch, "E28.32.11.0", {"start": v(-4.67, 7.81) * mm, "mid": v(-4.73, 7.86) * mm, "end": v(-4.8, 7.85) * mm});
            skLineSegment(sketch, "E28.36.11.0", {"start": v(-4.35, 7.28) * mm, "end": v(-4.67, 7.81) * mm});
            skArc(sketch, "E28.39.11.0", {"start": v(-4.37, 7.16) * mm, "mid": v(-4.34, 7.22) * mm, "end": v(-4.35, 7.28) * mm});
            skLineSegment(sketch, "E28.43.11.0", {"start": v(-5, 6.63) * mm, "end": v(-4.37, 7.16) * mm});
            skArc(sketch, "E28.46.11.0", {"start": v(-5, 6.63) * mm, "mid": v(-5.03, 6.56) * mm, "end": v(-5, 6.5) * mm});
            skSolve(sketch);
        }
        {
            var Q0;
            Q0 = qSketchRegion(id + "F16", true);
            extrude(context, id + "F17", {"entities" : qUnion([Q0]), "depth" : -5.5 * mm, "offsetDistance" : 25 * mm});
        }
        {
            var Q0;
            Q0=makeQuery(id+"F13.boolean.opBoolean","MERGE",FACE,{"derivedFrom":[makeQuery(id+"F1.opExtrude","CAP_FACE",FACE,{"disambiguationData":[OSD([sQuery(id+"F0.wireOp",EDGE,"E0")])],"isStart":true}),makeQuery(id+"F13.opExtrude","CAP_FACE",FACE,{"disambiguationData":[OSD([sQuery(id+"F12.wireOp",EDGE,"E12")])],"isStart":true})]});
            var sketch = newSketch(context, id + "F18", { "sketchPlane" : qUnion([Q0])});
            skLineSegment(sketch, "E29", {"start": v(0, 0) * mm, "end": v(11, 0) * mm});
            skLineSegment(sketch, "E30", {"start": v(0, 0) * mm, "end": v(0, -11) * mm});
            skSolve(sketch);
        }
        {
            var Q0;
            Q0=sQuery(id+"F18.wireOp",EDGE,"E30");
            cPlane(context, id + "F19", {"entities" : qUnion([Q0]), "cplaneType" : CPlaneType.LINE_ANGLE, "offset" : 25 * mm, "angle" : 80 * degree, "width" : 150 * mm, "height" : 150 * mm});
        }
        {
            var Q0;
            Q0=qCreatedBy(id+"F19.planeOp",FACE);
            cPlane(context, id + "F20", {"entities" : qUnion([Q0]), "cplaneType" : CPlaneType.OFFSET, "offset" : 12 * mm, "oppositeDirection" : true, "width" : 150 * mm, "height" : 150 * mm});
        }
        {
            var Q0;
            Q0=qCreatedBy(id+"F20.planeOp",FACE);
            var sketch = newSketch(context, id + "F21", { "sketchPlane" : qUnion([Q0])});
            skArc(sketch, "E31", {"start": v(4, 4.15) * mm, "mid": v(5.5, 5.65) * mm, "end": v(4, 7.15) * mm});
            skArc(sketch, "E32", {"start": v(-4, 7.15) * mm, "mid": v(-5.5, 5.65) * mm, "end": v(-4, 4.15) * mm});
            skLineSegment(sketch, "E33", {"start": v(4, 4.15) * mm, "end": v(-4, 4.15) * mm});
            skLineSegment(sketch, "E34", {"start": v(4, 7.15) * mm, "end": v(-4, 7.15) * mm});
            skSolve(sketch);
        }
        {
            var Q0;
            Q0 = qSketchRegion(id + "F21", true);
            extrude(context, id + "F22", {"entities" : qUnion([Q0]), "operationType" : NewBodyOperationType.REMOVE, "depth" : 5 * mm, "offsetDistance" : 25 * mm});
        }
        {
            var Q0;
            Q0=sQuery(id+"F18.wireOp",EDGE,"E30");
            cPlane(context, id + "F23", {"entities" : qUnion([Q0]), "cplaneType" : CPlaneType.LINE_ANGLE, "offset" : 25 * mm, "angle" : 80 * degree, "oppositeDirection" : true, "width" : 150 * mm, "height" : 150 * mm});
        }
        {
            var Q0;
            Q0=qCreatedBy(id+"F23.planeOp",FACE);
            cPlane(context, id + "F24", {"entities" : qUnion([Q0]), "cplaneType" : CPlaneType.OFFSET, "offset" : 12 * mm, "oppositeDirection" : true, "width" : 150 * mm, "height" : 150 * mm});
        }
        {
            var Q0;
            Q0=qCreatedBy(id+"F24.planeOp",FACE);
            var sketch = newSketch(context, id + "F25", { "sketchPlane" : qUnion([Q0])});
            skArc(sketch, "E35", {"start": v(-4, 7.15) * mm, "mid": v(-5.5, 5.65) * mm, "end": v(-4, 4.15) * mm});
            skArc(sketch, "E36", {"start": v(4, 4.15) * mm, "mid": v(5.5, 5.65) * mm, "end": v(4, 7.15) * mm});
            skLineSegment(sketch, "E37", {"start": v(-4, 7.15) * mm, "end": v(4, 7.15) * mm});
            skLineSegment(sketch, "E38", {"start": v(-4, 4.15) * mm, "end": v(4, 4.15) * mm});
            skSolve(sketch);
        }
        {
            var Q0;
            Q0=makeQuery(id+"F25.imprint","IMPRINT",FACE,{"disambiguationData":[TD([[makeQuery(id+"F25.imprint","IMPRINT",EDGE,{"derivedFrom":sQuery(id+"F25.wireOp",EDGE,"E35")}),1.0]])]});
            extrude(context, id + "F26", {"entities" : qUnion([Q0]), "operationType" : NewBodyOperationType.REMOVE, "depth" : 5 * mm, "offsetDistance" : 25 * mm});
        }
        {
            var Q0;
            Q0=sQuery(id+"F18.wireOp",EDGE,"E29");
            cPlane(context, id + "F27", {"entities" : qUnion([Q0]), "cplaneType" : CPlaneType.LINE_ANGLE, "offset" : 25 * mm, "angle" : 10 * degree, "oppositeDirection" : true, "width" : 150 * mm, "height" : 150 * mm});
        }
        {
            var Q0;
            Q0=qCreatedBy(id+"F27.planeOp",FACE);
            cPlane(context, id + "F28", {"entities" : qUnion([Q0]), "cplaneType" : CPlaneType.OFFSET, "offset" : 12 * mm, "width" : 150 * mm, "height" : 150 * mm});
        }
        {
            var Q0;
            Q0=qCreatedBy(id+"F28.planeOp",FACE);
            var sketch = newSketch(context, id + "F29", { "sketchPlane" : qUnion([Q0])});
            skArc(sketch, "E39", {"start": v(-4, 7.15) * mm, "mid": v(-5.5, 5.65) * mm, "end": v(-4, 4.15) * mm});
            skArc(sketch, "E40", {"start": v(4, 4.15) * mm, "mid": v(5.5, 5.65) * mm, "end": v(4, 7.15) * mm});
            skLineSegment(sketch, "E41", {"start": v(-4, 7.15) * mm, "end": v(4, 7.15) * mm});
            skLineSegment(sketch, "E42", {"start": v(-4, 4.15) * mm, "end": v(4, 4.15) * mm});
            skSolve(sketch);
        }
        {
            var Q0;
            Q0 = qSketchRegion(id + "F29", true);
            extrude(context, id + "F30", {"entities" : qUnion([Q0]), "operationType" : NewBodyOperationType.REMOVE, "oppositeDirection" : true, "depth" : 5 * mm, "offsetDistance" : 25 * mm});
        }
        {
            var Q0;
            Q0=sQuery(id+"F18.wireOp",EDGE,"E29");
            cPlane(context, id + "F31", {"entities" : qUnion([Q0]), "cplaneType" : CPlaneType.LINE_ANGLE, "offset" : 25 * mm, "angle" : 10 * degree, "width" : 150 * mm, "height" : 150 * mm});
        }
        {
            var Q0;
            Q0=qCreatedBy(id+"F31.planeOp",FACE);
            cPlane(context, id + "F32", {"entities" : qUnion([Q0]), "cplaneType" : CPlaneType.OFFSET, "offset" : 12 * mm, "oppositeDirection" : true, "width" : 150 * mm, "height" : 150 * mm});
        }
        {
            var Q0;
            Q0=qCreatedBy(id+"F32.planeOp",FACE);
            var sketch = newSketch(context, id + "F33", { "sketchPlane" : qUnion([Q0])});
            skArc(sketch, "E43", {"start": v(4, 4.15) * mm, "mid": v(5.5, 5.65) * mm, "end": v(4, 7.15) * mm});
            skArc(sketch, "E44", {"start": v(-4, 7.15) * mm, "mid": v(-5.5, 5.65) * mm, "end": v(-4, 4.15) * mm});
            skLineSegment(sketch, "E45", {"start": v(4, 4.15) * mm, "end": v(-4, 4.15) * mm});
            skLineSegment(sketch, "E46", {"start": v(4, 7.15) * mm, "end": v(-4, 7.15) * mm});
            skSolve(sketch);
        }
        {
            var Q0;
            Q0 = qSketchRegion(id + "F33", true);
            extrude(context, id + "F34", {"entities" : qUnion([Q0]), "operationType" : NewBodyOperationType.REMOVE, "depth" : 5 * mm, "offsetDistance" : 25 * mm});
        }
        {
            var Q0;
            Q0=makeQuery(id+"F17.opExtrude","CAP_FACE",FACE,{"disambiguationData":[OSD([sQuery(id+"F16.wireOp",EDGE,"E27.1.0"),sQuery(id+"F16.wireOp",EDGE,"E27.1.1"),sQuery(id+"F16.wireOp",EDGE,"E27.1.2"),sQuery(id+"F16.wireOp",EDGE,"E27.1.3"),sQuery(id+"F16.wireOp",EDGE,"E27.1.4"),sQuery(id+"F16.wireOp",EDGE,"E27.1.6"),sQuery(id+"F16.wireOp",EDGE,"E27.1.7"),sQuery(id+"F16.wireOp",EDGE,"E27.1.8"),sQuery(id+"F16.wireOp",EDGE,"E27.1.9"),sQuery(id+"F16.wireOp",EDGE,"E27.1.10"),sQuery(id+"F16.wireOp",EDGE,"E27.1.11"),sQuery(id+"F16.wireOp",EDGE,"E27.1.12"),sQuery(id+"F16.wireOp",EDGE,"E27.1.13"),sQuery(id+"F16.wireOp",EDGE,"E27.1.14")])],"isStart":true});
            var Q1;
            Q1=makeQuery(id+"F17.opExtrude","CAP_FACE",FACE,{"disambiguationData":[OSD([sQuery(id+"F16.wireOp",EDGE,"E13"),sQuery(id+"F16.wireOp",EDGE,"E14"),sQuery(id+"F16.wireOp",EDGE,"E15"),sQuery(id+"F16.wireOp",EDGE,"E16"),sQuery(id+"F16.wireOp",EDGE,"E17"),sQuery(id+"F16.wireOp",EDGE,"E18"),sQuery(id+"F16.wireOp",EDGE,"E19"),sQuery(id+"F16.wireOp",EDGE,"E20"),sQuery(id+"F16.wireOp",EDGE,"E21.filletArc"),sQuery(id+"F16.wireOp",EDGE,"E22.filletArc"),sQuery(id+"F16.wireOp",EDGE,"E23.filletArc"),sQuery(id+"F16.wireOp",EDGE,"E24.filletArc"),sQuery(id+"F16.wireOp",EDGE,"E25.filletArc"),sQuery(id+"F16.wireOp",EDGE,"E26.filletArc")])],"isStart":true});
            var Q2;
            Q2=makeQuery(id+"F17.opExtrude","CAP_FACE",FACE,{"disambiguationData":[OSD([sQuery(id+"F16.wireOp",EDGE,"E28.1.11.0"),sQuery(id+"F16.wireOp",EDGE,"E28.3.11.0"),sQuery(id+"F16.wireOp",EDGE,"E28.7.11.0"),sQuery(id+"F16.wireOp",EDGE,"E28.10.11.0"),sQuery(id+"F16.wireOp",EDGE,"E28.13.11.0"),sQuery(id+"F16.wireOp",EDGE,"E28.17.11.0"),sQuery(id+"F16.wireOp",EDGE,"E28.21.11.0"),sQuery(id+"F16.wireOp",EDGE,"E28.24.11.0"),sQuery(id+"F16.wireOp",EDGE,"E28.28.11.0"),sQuery(id+"F16.wireOp",EDGE,"E28.32.11.0"),sQuery(id+"F16.wireOp",EDGE,"E28.36.11.0"),sQuery(id+"F16.wireOp",EDGE,"E28.39.11.0"),sQuery(id+"F16.wireOp",EDGE,"E28.43.11.0"),sQuery(id+"F16.wireOp",EDGE,"E28.46.11.0")])],"isStart":true});
            var Q3;
            Q3=makeQuery(id+"F17.opExtrude","CAP_FACE",FACE,{"disambiguationData":[OSD([sQuery(id+"F16.wireOp",EDGE,"E28.1.10.0"),sQuery(id+"F16.wireOp",EDGE,"E28.3.10.0"),sQuery(id+"F16.wireOp",EDGE,"E28.7.10.0"),sQuery(id+"F16.wireOp",EDGE,"E28.10.10.0"),sQuery(id+"F16.wireOp",EDGE,"E28.13.10.0"),sQuery(id+"F16.wireOp",EDGE,"E28.17.10.0"),sQuery(id+"F16.wireOp",EDGE,"E28.21.10.0"),sQuery(id+"F16.wireOp",EDGE,"E28.24.10.0"),sQuery(id+"F16.wireOp",EDGE,"E28.28.10.0"),sQuery(id+"F16.wireOp",EDGE,"E28.32.10.0"),sQuery(id+"F16.wireOp",EDGE,"E28.36.10.0"),sQuery(id+"F16.wireOp",EDGE,"E28.39.10.0"),sQuery(id+"F16.wireOp",EDGE,"E28.43.10.0"),sQuery(id+"F16.wireOp",EDGE,"E28.46.10.0")])],"isStart":true});
            var Q4;
            Q4=makeQuery(id+"F17.opExtrude","CAP_FACE",FACE,{"disambiguationData":[OSD([sQuery(id+"F16.wireOp",EDGE,"E28.1.9.0"),sQuery(id+"F16.wireOp",EDGE,"E28.3.9.0"),sQuery(id+"F16.wireOp",EDGE,"E28.7.9.0"),sQuery(id+"F16.wireOp",EDGE,"E28.10.9.0"),sQuery(id+"F16.wireOp",EDGE,"E28.13.9.0"),sQuery(id+"F16.wireOp",EDGE,"E28.17.9.0"),sQuery(id+"F16.wireOp",EDGE,"E28.21.9.0"),sQuery(id+"F16.wireOp",EDGE,"E28.24.9.0"),sQuery(id+"F16.wireOp",EDGE,"E28.28.9.0"),sQuery(id+"F16.wireOp",EDGE,"E28.32.9.0"),sQuery(id+"F16.wireOp",EDGE,"E28.36.9.0"),sQuery(id+"F16.wireOp",EDGE,"E28.39.9.0"),sQuery(id+"F16.wireOp",EDGE,"E28.43.9.0"),sQuery(id+"F16.wireOp",EDGE,"E28.46.9.0")])],"isStart":true});
            var Q5;
            Q5=makeQuery(id+"F17.opExtrude","CAP_FACE",FACE,{"disambiguationData":[OSD([sQuery(id+"F16.wireOp",EDGE,"E28.1.8.0"),sQuery(id+"F16.wireOp",EDGE,"E28.3.8.0"),sQuery(id+"F16.wireOp",EDGE,"E28.7.8.0"),sQuery(id+"F16.wireOp",EDGE,"E28.10.8.0"),sQuery(id+"F16.wireOp",EDGE,"E28.13.8.0"),sQuery(id+"F16.wireOp",EDGE,"E28.17.8.0"),sQuery(id+"F16.wireOp",EDGE,"E28.21.8.0"),sQuery(id+"F16.wireOp",EDGE,"E28.24.8.0"),sQuery(id+"F16.wireOp",EDGE,"E28.28.8.0"),sQuery(id+"F16.wireOp",EDGE,"E28.32.8.0"),sQuery(id+"F16.wireOp",EDGE,"E28.36.8.0"),sQuery(id+"F16.wireOp",EDGE,"E28.39.8.0"),sQuery(id+"F16.wireOp",EDGE,"E28.43.8.0"),sQuery(id+"F16.wireOp",EDGE,"E28.46.8.0")])],"isStart":true});
            var Q6;
            Q6=makeQuery(id+"F17.opExtrude","CAP_FACE",FACE,{"disambiguationData":[OSD([sQuery(id+"F16.wireOp",EDGE,"E28.1.7.0"),sQuery(id+"F16.wireOp",EDGE,"E28.3.7.0"),sQuery(id+"F16.wireOp",EDGE,"E28.7.7.0"),sQuery(id+"F16.wireOp",EDGE,"E28.10.7.0"),sQuery(id+"F16.wireOp",EDGE,"E28.13.7.0"),sQuery(id+"F16.wireOp",EDGE,"E28.17.7.0"),sQuery(id+"F16.wireOp",EDGE,"E28.21.7.0"),sQuery(id+"F16.wireOp",EDGE,"E28.24.7.0"),sQuery(id+"F16.wireOp",EDGE,"E28.28.7.0"),sQuery(id+"F16.wireOp",EDGE,"E28.32.7.0"),sQuery(id+"F16.wireOp",EDGE,"E28.36.7.0"),sQuery(id+"F16.wireOp",EDGE,"E28.39.7.0"),sQuery(id+"F16.wireOp",EDGE,"E28.43.7.0"),sQuery(id+"F16.wireOp",EDGE,"E28.46.7.0")])],"isStart":true});
            var Q7;
            Q7=makeQuery(id+"F17.opExtrude","CAP_FACE",FACE,{"disambiguationData":[OSD([sQuery(id+"F16.wireOp",EDGE,"E28.1.6.0"),sQuery(id+"F16.wireOp",EDGE,"E28.3.6.0"),sQuery(id+"F16.wireOp",EDGE,"E28.7.6.0"),sQuery(id+"F16.wireOp",EDGE,"E28.10.6.0"),sQuery(id+"F16.wireOp",EDGE,"E28.13.6.0"),sQuery(id+"F16.wireOp",EDGE,"E28.17.6.0"),sQuery(id+"F16.wireOp",EDGE,"E28.21.6.0"),sQuery(id+"F16.wireOp",EDGE,"E28.24.6.0"),sQuery(id+"F16.wireOp",EDGE,"E28.28.6.0"),sQuery(id+"F16.wireOp",EDGE,"E28.32.6.0"),sQuery(id+"F16.wireOp",EDGE,"E28.36.6.0"),sQuery(id+"F16.wireOp",EDGE,"E28.39.6.0"),sQuery(id+"F16.wireOp",EDGE,"E28.43.6.0"),sQuery(id+"F16.wireOp",EDGE,"E28.46.6.0")])],"isStart":true});
            var Q8;
            Q8=makeQuery(id+"F17.opExtrude","CAP_FACE",FACE,{"disambiguationData":[OSD([sQuery(id+"F16.wireOp",EDGE,"E28.1.5.0"),sQuery(id+"F16.wireOp",EDGE,"E28.3.5.0"),sQuery(id+"F16.wireOp",EDGE,"E28.7.5.0"),sQuery(id+"F16.wireOp",EDGE,"E28.10.5.0"),sQuery(id+"F16.wireOp",EDGE,"E28.13.5.0"),sQuery(id+"F16.wireOp",EDGE,"E28.17.5.0"),sQuery(id+"F16.wireOp",EDGE,"E28.21.5.0"),sQuery(id+"F16.wireOp",EDGE,"E28.24.5.0"),sQuery(id+"F16.wireOp",EDGE,"E28.28.5.0"),sQuery(id+"F16.wireOp",EDGE,"E28.32.5.0"),sQuery(id+"F16.wireOp",EDGE,"E28.36.5.0"),sQuery(id+"F16.wireOp",EDGE,"E28.39.5.0"),sQuery(id+"F16.wireOp",EDGE,"E28.43.5.0"),sQuery(id+"F16.wireOp",EDGE,"E28.46.5.0")])],"isStart":true});
            var Q9;
            Q9=makeQuery(id+"F17.opExtrude","CAP_FACE",FACE,{"disambiguationData":[OSD([sQuery(id+"F16.wireOp",EDGE,"E28.1.4.0"),sQuery(id+"F16.wireOp",EDGE,"E28.3.4.0"),sQuery(id+"F16.wireOp",EDGE,"E28.7.4.0"),sQuery(id+"F16.wireOp",EDGE,"E28.10.4.0"),sQuery(id+"F16.wireOp",EDGE,"E28.13.4.0"),sQuery(id+"F16.wireOp",EDGE,"E28.17.4.0"),sQuery(id+"F16.wireOp",EDGE,"E28.21.4.0"),sQuery(id+"F16.wireOp",EDGE,"E28.24.4.0"),sQuery(id+"F16.wireOp",EDGE,"E28.28.4.0"),sQuery(id+"F16.wireOp",EDGE,"E28.32.4.0"),sQuery(id+"F16.wireOp",EDGE,"E28.36.4.0"),sQuery(id+"F16.wireOp",EDGE,"E28.39.4.0"),sQuery(id+"F16.wireOp",EDGE,"E28.43.4.0"),sQuery(id+"F16.wireOp",EDGE,"E28.46.4.0")])],"isStart":true});
            var Q10;
            Q10=makeQuery(id+"F17.opExtrude","CAP_FACE",FACE,{"disambiguationData":[OSD([sQuery(id+"F16.wireOp",EDGE,"E28.1.3.0"),sQuery(id+"F16.wireOp",EDGE,"E28.3.3.0"),sQuery(id+"F16.wireOp",EDGE,"E28.7.3.0"),sQuery(id+"F16.wireOp",EDGE,"E28.10.3.0"),sQuery(id+"F16.wireOp",EDGE,"E28.13.3.0"),sQuery(id+"F16.wireOp",EDGE,"E28.17.3.0"),sQuery(id+"F16.wireOp",EDGE,"E28.21.3.0"),sQuery(id+"F16.wireOp",EDGE,"E28.24.3.0"),sQuery(id+"F16.wireOp",EDGE,"E28.28.3.0"),sQuery(id+"F16.wireOp",EDGE,"E28.32.3.0"),sQuery(id+"F16.wireOp",EDGE,"E28.36.3.0"),sQuery(id+"F16.wireOp",EDGE,"E28.39.3.0"),sQuery(id+"F16.wireOp",EDGE,"E28.43.3.0"),sQuery(id+"F16.wireOp",EDGE,"E28.46.3.0")])],"isStart":true});
            var Q11;
            Q11=makeQuery(id+"F17.opExtrude","CAP_FACE",FACE,{"disambiguationData":[OSD([sQuery(id+"F16.wireOp",EDGE,"E27.2.0"),sQuery(id+"F16.wireOp",EDGE,"E27.2.1"),sQuery(id+"F16.wireOp",EDGE,"E27.2.2"),sQuery(id+"F16.wireOp",EDGE,"E27.2.3"),sQuery(id+"F16.wireOp",EDGE,"E27.2.4"),sQuery(id+"F16.wireOp",EDGE,"E27.2.6"),sQuery(id+"F16.wireOp",EDGE,"E27.2.7"),sQuery(id+"F16.wireOp",EDGE,"E27.2.8"),sQuery(id+"F16.wireOp",EDGE,"E27.2.9"),sQuery(id+"F16.wireOp",EDGE,"E27.2.10"),sQuery(id+"F16.wireOp",EDGE,"E27.2.11"),sQuery(id+"F16.wireOp",EDGE,"E27.2.12"),sQuery(id+"F16.wireOp",EDGE,"E27.2.13"),sQuery(id+"F16.wireOp",EDGE,"E27.2.14")])],"isStart":true});
            fillet(context, id + "F35", {"entities" : qUnion([Q0, Q1, Q2, Q3, Q4, Q5, Q6, Q7, Q8, Q9, Q10, Q11]), "radius" : .1 * mm, "tangentPropagation" : true, "allowEdgeOverflow" : false});
        }
    });
